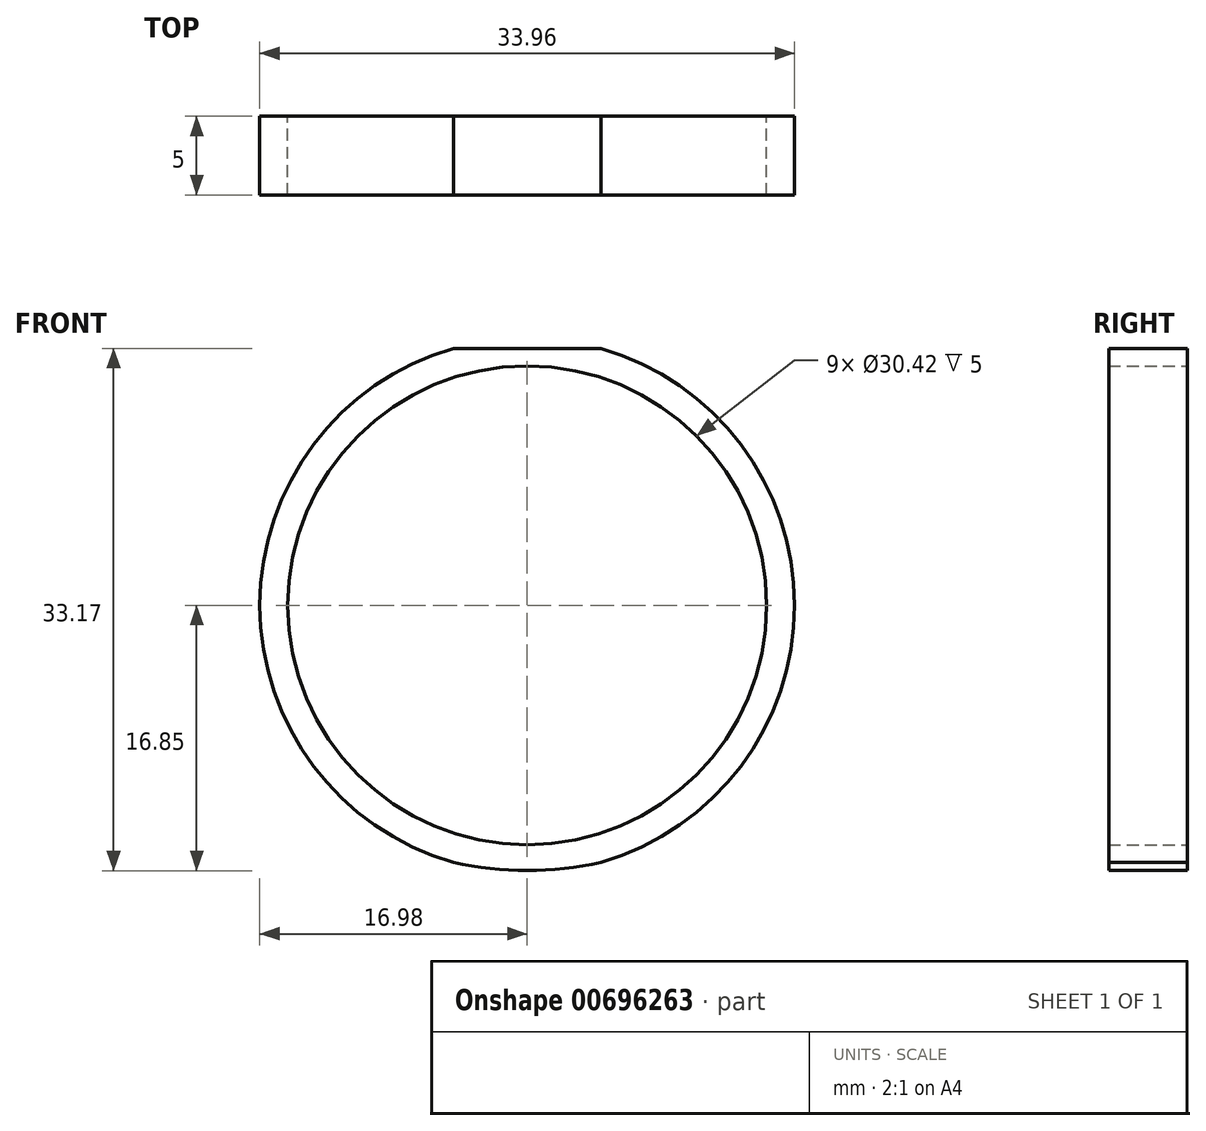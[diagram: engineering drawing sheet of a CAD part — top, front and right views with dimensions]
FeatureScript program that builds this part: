
annotation { "Feature Type Name" : "Feature", "Feature Type Description" : "" }
export const myFeature = defineFeature(function(context is Context, id is Id, definition is map)
    precondition{}
    {
        {
            var Q0;
            Q0=qCreatedBy(makeId("Front.planeOp"),FACE);
            var sketch = newSketch(context, id + "F0", { "sketchPlane" : qUnion([Q0])});
            skArc(sketch, "E0", {"start": v(-4.69, 16.32) * mm, "mid": v(-16.98, 0) * mm, "end": v(-4.69, -16.32) * mm});
            skCircle(sketch, "E1", {"center": v(0, 0) * mm, "radius": 15.2 * mm});
            skArc(sketch, "E2.trimOffspring", {"start": v(4.69, -16.32) * mm, "mid": v(16.98, 0) * mm, "end": v(4.69, 16.32) * mm});
            skLineSegment(sketch, "E3", {"start": v(-4.69, 16.32) * mm, "end": v(4.69, 16.32) * mm});
            skArc(sketch, "E4", {"start": v(-4.69, -16.32) * mm, "mid": v(0, -16.85) * mm, "end": v(4.69, -16.32) * mm});
            skSolve(sketch);
        }
        {
            var Q0;
            Q0=makeQuery(id+"F0.imprint","IMPRINT",FACE,{"disambiguationData":[TD([[makeQuery(id+"F0.imprint","IMPRINT",EDGE,{"derivedFrom":sQuery(id+"F0.wireOp",EDGE,"E0")}),1.0]])]});
            extrude(context, id + "F1", {"entities" : qUnion([Q0]), "depth" : 5 * mm, "offsetDistance" : 25 * mm});
        }
    });
